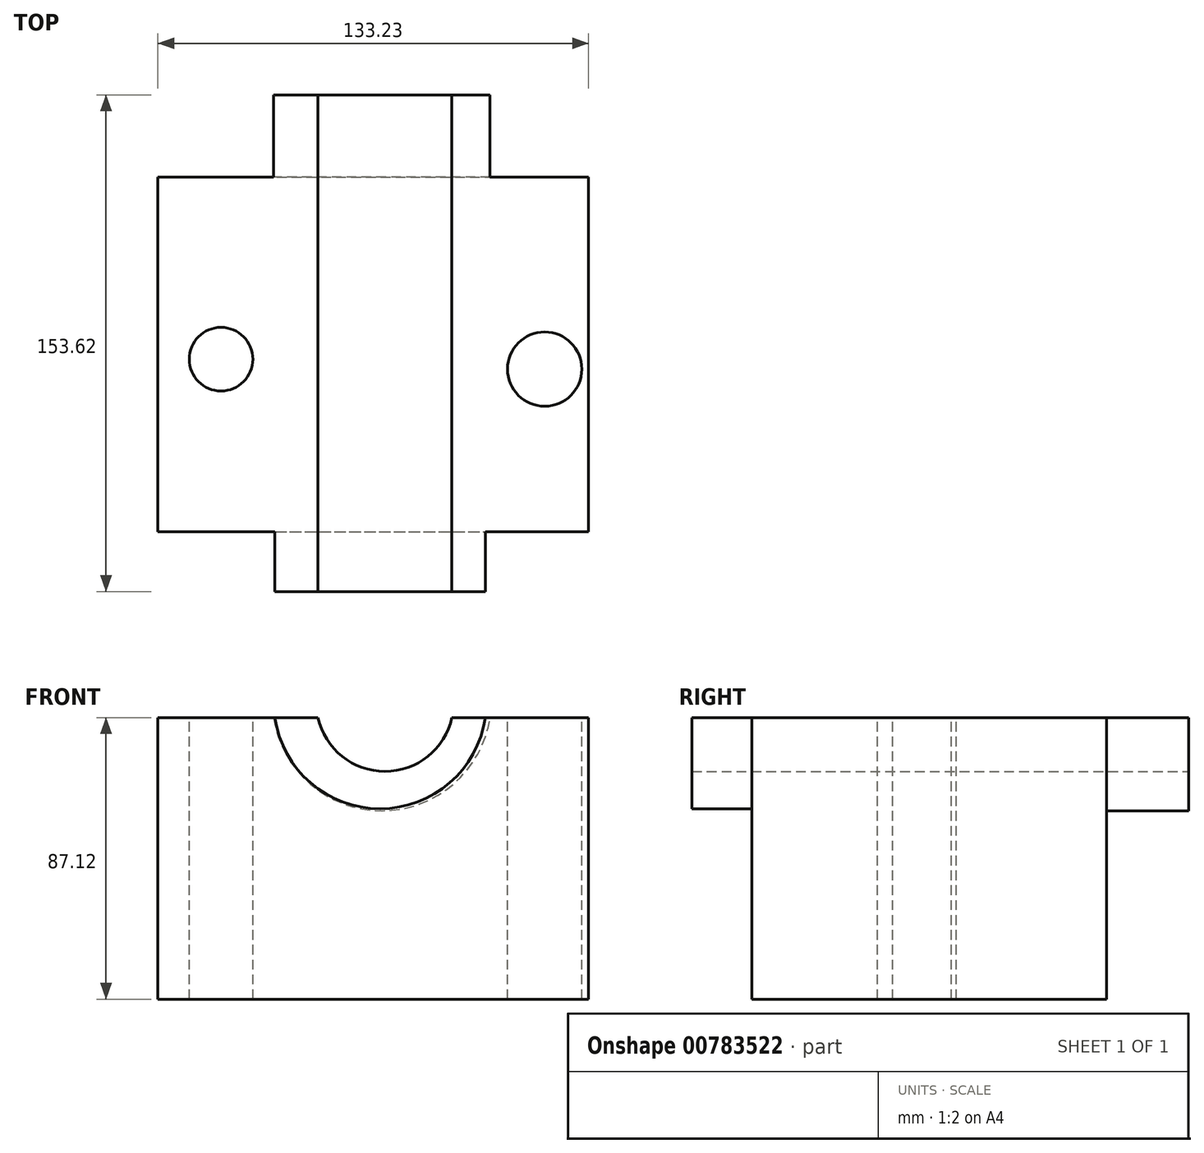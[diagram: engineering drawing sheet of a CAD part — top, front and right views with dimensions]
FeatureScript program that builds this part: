
annotation { "Feature Type Name" : "Feature", "Feature Type Description" : "" }
export const myFeature = defineFeature(function(context is Context, id is Id, definition is map)
    precondition{}
    {
        {
            var Q0;
            Q0=qCreatedBy(makeId("Top.planeOp"),FACE);
            var sketch = newSketch(context, id + "F0", { "sketchPlane" : qUnion([Q0])});
            skLineSegment(sketch, "E0.bottom", {"start": v(-69.9, -50.27) * mm, "end": v(63.33, -50.27) * mm});
            skLineSegment(sketch, "E0.top", {"start": v(-69.9, 59.41) * mm, "end": v(63.33, 59.41) * mm});
            skLineSegment(sketch, "E0.left", {"start": v(-69.9, -50.27) * mm, "end": v(-69.9, 59.41) * mm});
            skLineSegment(sketch, "E0.right", {"start": v(63.33, -50.27) * mm, "end": v(63.33, 59.41) * mm});
            skSolve(sketch);
        }
        {
            var Q0;
            Q0=makeQuery(id+"F0.imprint","IMPRINT",FACE,{"disambiguationData":[TD([[makeQuery(id+"F0.imprint","IMPRINT",EDGE,{"derivedFrom":sQuery(id+"F0.wireOp",EDGE,"E0.bottom")}),1.0]])]});
            extrude(context, id + "F1", {"entities" : qUnion([Q0]), "depth" : 87.12 * mm, "offsetDistance" : 25.4 * mm});
        }
        {
            var Q0;
            Q0=makeQuery(id+"F1.opExtrude","SWEPT_FACE",FACE,{"disambiguationData":[OSD([sQuery(id+"F0.wireOp",EDGE,"E0.bottom")])]});
            var sketch = newSketch(context, id + "F2", { "sketchPlane" : qUnion([Q0])});
            skArc(sketch, "E1", {"start": v(-33.7, 87.12) * mm, "mid": v(-1.15, 58.9) * mm, "end": v(31.4, 87.12) * mm});
            skArc(sketch, "E2", {"start": v(-20.33, 87.12) * mm, "mid": v(0.36, 70.45) * mm, "end": v(21.05, 87.12) * mm});
            skSolve(sketch);
        }
        {
            var Q0;
            {var subQ0=sQuery(id+"F2.wireOp",EDGE,"E1");Q0=makeQuery(id+"F2.imprint","IMPRINT",FACE,{"disambiguationData":[TD([[makeQuery(id+"F2.imprint","IMPRINT",EDGE,{"derivedFrom":subQ0}),1.0]])]});}
            extrude(context, id + "F3", {"entities" : qUnion([Q0]), "operationType" : NewBodyOperationType.ADD, "depth" : 18.54 * mm, "offsetDistance" : 25.4 * mm});
        }
        {
            var Q0;
            {var subQ0=sQuery(id+"F0.wireOp",EDGE,"E0.bottom");var subQ3=sQuery(id+"F2.wireOp",EDGE,"E2");Q0=makeQuery(id+"F3.boolean.opBoolean","SPLIT",FACE,{"disambiguationData":[TD([makeQuery(id+"F3.opExtrude","SWEPT_FACE",FACE,{"disambiguationData":[OSD([subQ3])]})])],"derivedFrom":makeQuery(id+"F1.opExtrude","SWEPT_FACE",FACE,{"disambiguationData":[OSD([subQ0])]})});}
            extrude(context, id + "F4", {"entities" : qUnion([Q0]), "operationType" : NewBodyOperationType.REMOVE, "oppositeDirection" : true, "depth" : 140.2 * mm, "offsetDistance" : 25.4 * mm});
        }
        {
            var Q0;
            Q0=makeQuery(id+"F1.opExtrude","SWEPT_FACE",FACE,{"disambiguationData":[OSD([sQuery(id+"F0.wireOp",EDGE,"E0.top")])]});
            var sketch = newSketch(context, id + "F5", { "sketchPlane" : qUnion([Q0])});
            skArc(sketch, "E3", {"start": v(-32.88, 87.12) * mm, "mid": v(0.6, 58.3) * mm, "end": v(34.07, 87.12) * mm});
            skSolve(sketch);
        }
        {
            var Q0;
            {var subQ0=sQuery(id+"F5.wireOp",EDGE,"E3");Q0=makeQuery(id+"F5.imprint","IMPRINT",FACE,{"disambiguationData":[TD([[makeQuery(id+"F5.imprint","IMPRINT",EDGE,{"derivedFrom":subQ0}),1.0]])]});}
            extrude(context, id + "F6", {"entities" : qUnion([Q0]), "operationType" : NewBodyOperationType.ADD, "depth" : 25.4 * mm, "offsetDistance" : 25.4 * mm});
        }
        {
            var Q0;
            {var subQ2=sQuery(id+"F0.wireOp",EDGE,"E0.left");var subQ3=makeQuery(id+"F1.opExtrude","SWEPT_FACE",FACE,{"disambiguationData":[OSD([subQ2])]});var subQ4=sQuery(id+"F0.wireOp",EDGE,"E0.top");var subQ6=sQuery(id+"F0.wireOp",EDGE,"E0.bottom");var subQ7=makeQuery(id+"F1.opExtrude","CAP_FACE",FACE,{"disambiguationData":[OSD([subQ6,subQ4,subQ2,sQuery(id+"F0.wireOp",EDGE,"E0.right")])],"isStart":false});var subQ8=sQuery(id+"F2.wireOp",EDGE,"E1");var subQ9=makeQuery(id+"F1.opExtrude","CAP_EDGE",EDGE,{"disambiguationData":[OSD([subQ6])],"isStart":false});var subQ10=makeQuery(id+"F3.opExtrude","SWEPT_FACE",FACE,{"disambiguationData":[OSD([subQ6]),TDD([makeQuery(id+"F2.imprint","IMPRINT",EDGE,{"disambiguationData":[TD([[makeQuery(id+"F2.imprint","INTERSECT",VERTEX,{"disambiguationData":[OD(0.0)],"derivedFrom":[subQ9,subQ8]}),-1.0]])],"derivedFrom":subQ9})])]});var subQ11=makeQuery(id+"F3.opExtrude","SWEPT_FACE",FACE,{"disambiguationData":[OSD([subQ6]),TDD([makeQuery(id+"F2.imprint","IMPRINT",EDGE,{"disambiguationData":[TD([[makeQuery(id+"F2.imprint","INTERSECT",VERTEX,{"disambiguationData":[OD(1.0)],"derivedFrom":[subQ9,subQ8]}),1.0]])],"derivedFrom":subQ9})])]});var subQ13=makeQuery(id+"F4.boolean.opBoolean","SPLIT",EDGE,{"disambiguationData":[TD([subQ3])],"derivedFrom":makeQuery(id+"F1.opExtrude","CAP_EDGE",EDGE,{"disambiguationData":[OSD([subQ4])],"isStart":false})});Q0=makeQuery(id+"F6.boolean.opBoolean","MERGE",FACE,{"derivedFrom":[makeQuery(id+"F4.boolean.opBoolean","SPLIT",FACE,{"disambiguationData":[TD([subQ3])],"derivedFrom":makeQuery(id+"F3.boolean.opBoolean","MERGE",FACE,{"derivedFrom":[subQ7,subQ10,subQ11]})}),makeQuery(id+"F6.opExtrude","SWEPT_FACE",FACE,{"disambiguationData":[OSD([subQ4]),TDD([makeQuery(id+"F5.imprint","IMPRINT",EDGE,{"disambiguationData":[TD([[makeQuery(id+"F5.imprint","INTERSECT",VERTEX,{"derivedFrom":[subQ13,sQuery(id+"F5.wireOp",EDGE,"E3")]}),-1.0]])],"derivedFrom":subQ13})])]})]});}
            var sketch = newSketch(context, id + "F7", { "sketchPlane" : qUnion([Q0])});
            skCircle(sketch, "E4", {"center": v(-50.35, 3.07) * mm, "radius": 9.84 * mm});
            skCircle(sketch, "E5", {"center": v(49.77, 0) * mm, "radius": 11.5 * mm});
            skSolve(sketch);
        }
        {
            var Q0;
            Q0=makeQuery(id+"F7.imprint","IMPRINT",FACE,{"disambiguationData":[TD([[makeQuery(id+"F7.imprint","IMPRINT",EDGE,{"derivedFrom":sQuery(id+"F7.wireOp",EDGE,"E4")}),1.0]])]});
            extrude(context, id + "F8", {"entities" : qUnion([Q0]), "operationType" : NewBodyOperationType.REMOVE, "oppositeDirection" : true, "depth" : 150.88 * mm, "offsetDistance" : 25.4 * mm});
        }
        {
            var Q0;
            Q0=makeQuery(id+"F7.imprint","IMPRINT",FACE,{"disambiguationData":[TD([[makeQuery(id+"F7.imprint","IMPRINT",EDGE,{"derivedFrom":sQuery(id+"F7.wireOp",EDGE,"E5")}),1.0]])]});
            extrude(context, id + "F9", {"entities" : qUnion([Q0]), "operationType" : NewBodyOperationType.REMOVE, "oppositeDirection" : true, "depth" : 154.43 * mm, "offsetDistance" : 25.4 * mm});
        }
    });
